# Revit family: for update_48491XXX_NEW
name_source: partatom
category: Plumbing Fixtures
revit_build: Autodesk Revit 2018 (Build: 20170223_1515(x64)
units: mm (PartAtom-declared; Revit-internal decimal feet)

## family parameters
Always vertical = No
Cut with Voids When Loaded = No
OmniClass Number = 23.31.17.00
OmniClass Title = Showers
Part Type = Normal
Room Calculation Point = No
Round Connector Dimension = Use Diameter
Shared = No
Work Plane-Based = Yes

## types (1)
- Default - please load Revit Family Type Catalog
    Always visible = Yes
    BIMobject category = Showers
    Connector Description = Water Inlet 12.7mm
    Date of publishing = 9/28/2022 12:00:00 AM
    Default Elevation = 1219.2 mm  [stored 4 ft]
    Description = AXOR One Overhead shower 280 1jet with shower arm
    Diameter = 13 mm
    EAN code = 4059625469484
    Edition number = 1
    GTIN code = https://4059625469484
    IFC Classification = Sanitary Terminal
    Manufacturer = AXOR
    Manufacturer name = AXOR
    Masterformat 2014 Code = 22 41 23
    Masterformat 2014 Description = Residential Showers
    Material 1 = AXOR - Metal - 000 Chrome
    Material 2 = AXOR - Plastic - Graphite
    Model = 48491XXX
    OmniClass Code = 23-31 17 00
    OmniClass Description = Showers
    Product Guid = c5b648d2-0937-4433-8721-0cec2c6381aa
    Product SKU = 48491XXX
    Product data url = https://bimobject.com
    Product family = AXOR One
    Product group = Overhead showers
    Product name = 48491XXX AXOR One Overhead shower 280 1jet with shower arm
    Product url = https://www.axor-design.com
    QR code = https://bimobject.com
    UNSPSC Code = 30181503
    URL = https://www.axor-design.com
    Uniclass 2015 Code = Pr_40_20_87_76
    Uniclass 2015 Name = Shower heads
    Uniformat II Code = D2010
    Uniformat II Description = Plumbing Fixtures
    Weight Net (Kg) = 4.8

note: [stored X ft] marks values corroborated as IEEE doubles in the binary element streams (Revit-internal decimal feet)

## geometry (parser evidence)
native form markers: Sweep x2
no freeform markers — native parametric forms only
